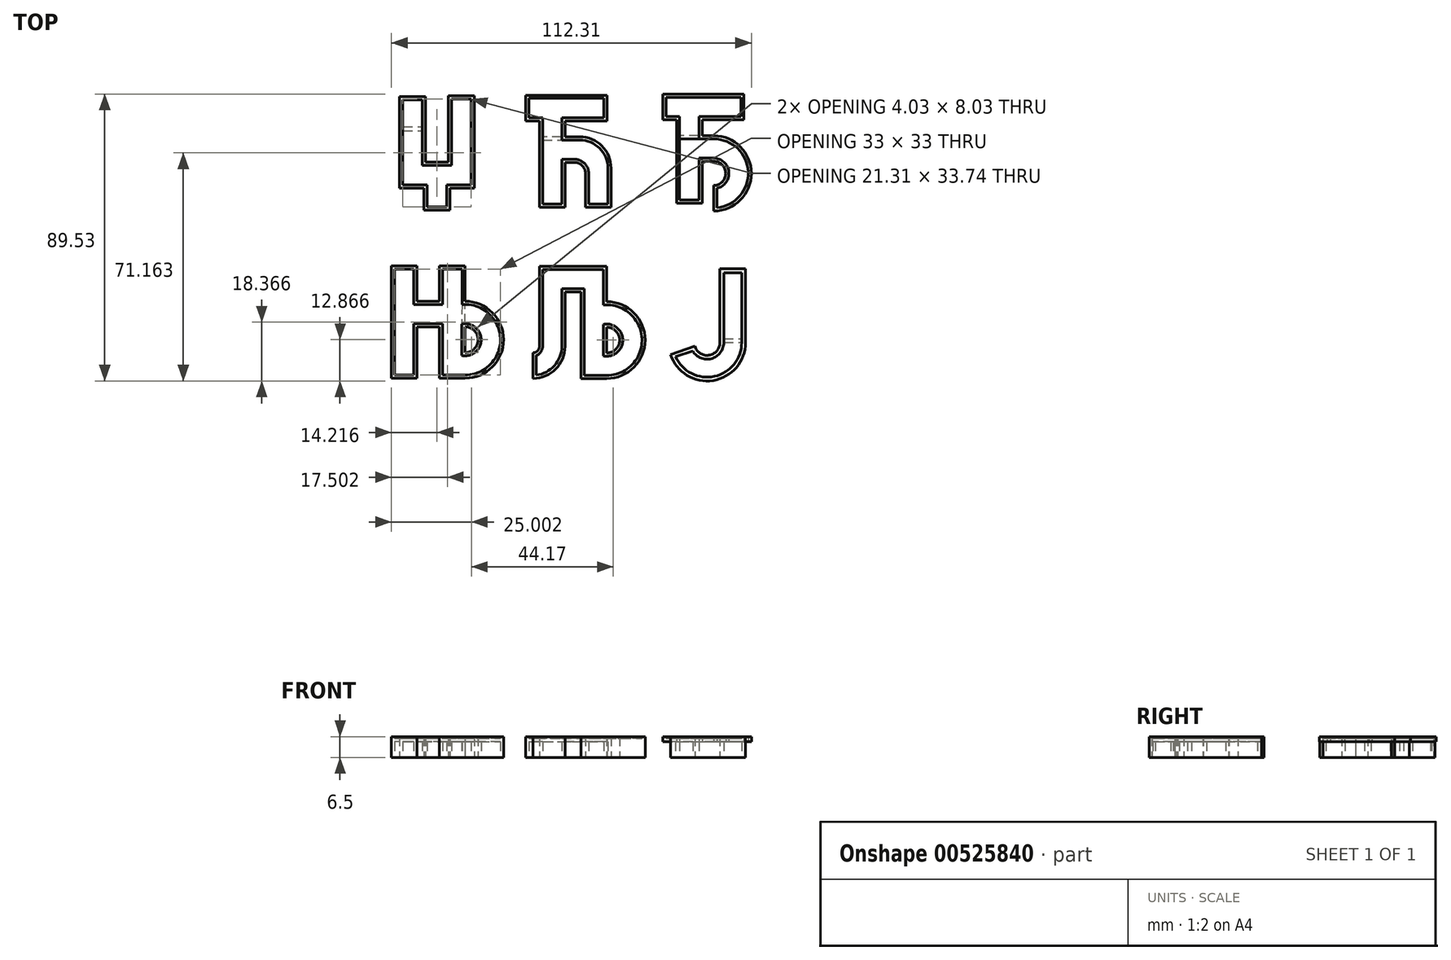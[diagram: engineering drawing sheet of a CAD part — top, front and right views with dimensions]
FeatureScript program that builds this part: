
annotation { "Feature Type Name" : "Feature", "Feature Type Description" : "" }
export const myFeature = defineFeature(function(context is Context, id is Id, definition is map)
    precondition{}
    {
        {
            var Q0;
            Q0=qCreatedBy(makeId("Top.planeOp"),FACE);
            var sketch = newSketch(context, id + "F0", { "sketchPlane" : qUnion([Q0])});
            skLineSegment(sketch, "E0", {"start": v(-54.27, 17.56) * mm, "end": v(-54.27, 46.23) * mm});
            skLineSegment(sketch, "E1", {"start": v(-54.27, 46.23) * mm, "end": v(-46.16, 46.23) * mm});
            skLineSegment(sketch, "E2", {"start": v(-46.16, 46.23) * mm, "end": v(-46.16, 25.68) * mm});
            skLineSegment(sketch, "E3", {"start": v(-46.16, 25.68) * mm, "end": v(-39.05, 25.68) * mm});
            skLineSegment(sketch, "E4", {"start": v(-39.05, 25.68) * mm, "end": v(-39.05, 46.48) * mm});
            skLineSegment(sketch, "E5", {"start": v(-39.05, 46.48) * mm, "end": v(-30.93, 46.48) * mm});
            skLineSegment(sketch, "E6", {"start": v(-30.93, 46.48) * mm, "end": v(-30.93, 17.56) * mm});
            skLineSegment(sketch, "E7", {"start": v(-30.93, 17.56) * mm, "end": v(-38.55, 17.56) * mm});
            skLineSegment(sketch, "E8", {"start": v(-38.55, 17.56) * mm, "end": v(-38.55, 10.7) * mm});
            skLineSegment(sketch, "E9", {"start": v(-38.55, 10.7) * mm, "end": v(-46.66, 10.7) * mm});
            skLineSegment(sketch, "E10", {"start": v(-46.66, 10.7) * mm, "end": v(-46.66, 17.56) * mm});
            skLineSegment(sketch, "E11", {"start": v(-46.66, 17.56) * mm, "end": v(-54.27, 17.56) * mm});
            skLineSegment(sketch, "E12.0", {"start": v(-31.95, 18.57) * mm, "end": v(-39.56, 18.57) * mm});
            skLineSegment(sketch, "E12.1", {"start": v(-53.26, 18.57) * mm, "end": v(-53.26, 45.21) * mm});
            skLineSegment(sketch, "E12.2", {"start": v(-45.65, 18.57) * mm, "end": v(-53.26, 18.57) * mm});
            skLineSegment(sketch, "E12.3", {"start": v(-45.65, 11.72) * mm, "end": v(-45.65, 18.57) * mm});
            skLineSegment(sketch, "E12.4", {"start": v(-39.56, 11.72) * mm, "end": v(-45.65, 11.72) * mm});
            skLineSegment(sketch, "E12.5", {"start": v(-53.26, 45.21) * mm, "end": v(-47.17, 45.21) * mm});
            skLineSegment(sketch, "E12.6", {"start": v(-39.56, 18.57) * mm, "end": v(-39.56, 11.72) * mm});
            skLineSegment(sketch, "E12.7", {"start": v(-47.17, 45.21) * mm, "end": v(-47.17, 24.66) * mm});
            skLineSegment(sketch, "E12.8", {"start": v(-47.17, 24.66) * mm, "end": v(-38.04, 24.66) * mm});
            skLineSegment(sketch, "E12.9", {"start": v(-38.04, 24.66) * mm, "end": v(-38.04, 45.46) * mm});
            skLineSegment(sketch, "E12.10", {"start": v(-38.04, 45.46) * mm, "end": v(-31.95, 45.46) * mm});
            skLineSegment(sketch, "E12.11", {"start": v(-31.95, 45.46) * mm, "end": v(-31.95, 18.57) * mm});
            skLineSegment(sketch, "E13", {"start": v(-53.26, 36.84) * mm, "end": v(-47.17, 36.84) * mm});
            skLineSegment(sketch, "E14", {"start": v(-53.26, 35.56) * mm, "end": v(-47.17, 35.56) * mm});
            skLineSegment(sketch, "E15", {"start": v(-45.65, 24.66) * mm, "end": v(-47.17, 24.66) * mm});
            skSolve(sketch);
        }
        {
            var Q0;
            Q0 = qSketchRegion(id + "F0", true);
            var Q1;
            Q1=makeQuery(id+"F0.imprint","IMPRINT",FACE,{"disambiguationData":[TD([[makeQuery(id+"F0.imprint","IMPRINT",EDGE,{"derivedFrom":sQuery(id+"F0.wireOp",EDGE,"E12.0")}),-1.0]])]});
            var Q2;
            {var subQ0=sQuery(id+"F0.wireOp",EDGE,"E13");Q2=makeQuery(id+"F0.imprint","IMPRINT",FACE,{"disambiguationData":[TD([[makeQuery(id+"F0.imprint","IMPRINT",EDGE,{"derivedFrom":subQ0}),-1.0]])]});}
            var Q3;
            {var subQ0=sQuery(id+"F0.wireOp",EDGE,"E12.5");Q3=makeQuery(id+"F0.imprint","IMPRINT",FACE,{"disambiguationData":[TD([[makeQuery(id+"F0.imprint","IMPRINT",EDGE,{"derivedFrom":subQ0}),-1.0]])]});}
            extrude(context, id + "F1", {"entities" : qUnion([Q0, Q1, Q2, Q3]), "depth" : 6 * mm, "offsetDistance" : 25 * mm});
        }
        {
            var Q0;
            Q0=makeQuery(id+"F0.imprint","IMPRINT",FACE,{"disambiguationData":[TD([[makeQuery(id+"F0.imprint","IMPRINT",EDGE,{"derivedFrom":sQuery(id+"F0.wireOp",EDGE,"E0")}),-1.0]])]});
            extrude(context, id + "F2", {"entities" : qUnion([Q0]), "operationType" : NewBodyOperationType.ADD, "depth" : 6.5 * mm, "offsetDistance" : 25 * mm});
        }
        {
            var Q0;
            Q0=makeQuery(id+"F0.imprint","IMPRINT",FACE,{"disambiguationData":[TD([[makeQuery(id+"F0.imprint","IMPRINT",EDGE,{"derivedFrom":sQuery(id+"F0.wireOp",EDGE,"E12.0")}),-1.0]])]});
            var Q1;
            {var subQ0=sQuery(id+"F0.wireOp",EDGE,"E12.5");Q1=makeQuery(id+"F0.imprint","IMPRINT",FACE,{"disambiguationData":[TD([[makeQuery(id+"F0.imprint","IMPRINT",EDGE,{"derivedFrom":subQ0}),-1.0]])]});}
            extrude(context, id + "F3", {"entities" : qUnion([Q0, Q1]), "operationType" : NewBodyOperationType.REMOVE, "depth" : 5 * mm, "offsetDistance" : 25 * mm});
        }
        {
            var Q0;
            Q0=qCreatedBy(makeId("Top.planeOp"),FACE);
            var sketch = newSketch(context, id + "F4", { "sketchPlane" : qUnion([Q0])});
            skLineSegment(sketch, "E16", {"start": v(-10.68, 38.61) * mm, "end": v(-10.68, 11.61) * mm});
            skLineSegment(sketch, "E17", {"start": v(-10.68, 11.61) * mm, "end": v(-2.68, 11.61) * mm});
            skLineSegment(sketch, "E18", {"start": v(-2.68, 11.61) * mm, "end": v(-2.68, 25.61) * mm});
            skLineSegment(sketch, "E19", {"start": v(-2.68, 25.61) * mm, "end": v(0.33, 25.61) * mm});
            skLineSegment(sketch, "E20", {"start": v(-10.68, 38.61) * mm, "end": v(-14.93, 38.61) * mm});
            skLineSegment(sketch, "E21", {"start": v(-14.93, 38.61) * mm, "end": v(-14.93, 46.61) * mm});
            skLineSegment(sketch, "E22", {"start": v(-14.93, 46.61) * mm, "end": v(10.4, 46.61) * mm});
            skLineSegment(sketch, "E23", {"start": v(10.4, 46.61) * mm, "end": v(10.4, 38.61) * mm});
            skLineSegment(sketch, "E24", {"start": v(10.4, 38.61) * mm, "end": v(-2.68, 38.61) * mm});
            skLineSegment(sketch, "E25", {"start": v(-2.68, 38.61) * mm, "end": v(-2.68, 33.61) * mm});
            skLineSegment(sketch, "E26", {"start": v(-2.68, 33.61) * mm, "end": v(1.92, 33.61) * mm});
            skArc(sketch, "E27", {"start": v(0.33, 25.61) * mm, "mid": v(2.86, 24.48) * mm, "end": v(3.7, 21.84) * mm});
            skArc(sketch, "E28", {"start": v(1.92, 33.61) * mm, "mid": v(8.84, 30.75) * mm, "end": v(11.7, 23.83) * mm});
            skLineSegment(sketch, "E29", {"start": v(3.7, 21.84) * mm, "end": v(3.7, 11.61) * mm});
            skLineSegment(sketch, "E30", {"start": v(11.7, 11.61) * mm, "end": v(11.7, 23.83) * mm});
            skLineSegment(sketch, "E31", {"start": v(11.7, 11.61) * mm, "end": v(3.7, 11.61) * mm});
            skLineSegment(sketch, "E32.0", {"start": v(9.4, 39.61) * mm, "end": v(-3.68, 39.61) * mm});
            skLineSegment(sketch, "E32.1", {"start": v(9.4, 45.61) * mm, "end": v(9.4, 39.61) * mm});
            skLineSegment(sketch, "E32.2", {"start": v(-13.93, 45.61) * mm, "end": v(9.4, 45.61) * mm});
            skLineSegment(sketch, "E32.3", {"start": v(-13.93, 39.61) * mm, "end": v(-13.93, 45.61) * mm});
            skLineSegment(sketch, "E32.4", {"start": v(-9.68, 39.61) * mm, "end": v(-13.93, 39.61) * mm});
            skLineSegment(sketch, "E32.5", {"start": v(10.7, 12.61) * mm, "end": v(4.7, 12.61) * mm});
            skLineSegment(sketch, "E32.6", {"start": v(10.7, 12.61) * mm, "end": v(10.7, 23.83) * mm});
            skArc(sketch, "E32.7", {"start": v(1.92, 32.61) * mm, "mid": v(8.13, 30.04) * mm, "end": v(10.7, 23.83) * mm});
            skLineSegment(sketch, "E32.8", {"start": v(-3.68, 32.61) * mm, "end": v(1.92, 32.61) * mm});
            skLineSegment(sketch, "E32.9", {"start": v(4.7, 21.8) * mm, "end": v(4.7, 12.61) * mm});
            skArc(sketch, "E32.10", {"start": v(0.33, 26.61) * mm, "mid": v(3.58, 25.17) * mm, "end": v(4.7, 21.8) * mm});
            skLineSegment(sketch, "E32.11", {"start": v(-3.68, 26.61) * mm, "end": v(0.33, 26.61) * mm});
            skLineSegment(sketch, "E32.12", {"start": v(-3.68, 12.61) * mm, "end": v(-3.68, 26.61) * mm});
            skLineSegment(sketch, "E32.13", {"start": v(-9.68, 12.61) * mm, "end": v(-3.68, 12.61) * mm});
            skLineSegment(sketch, "E32.14", {"start": v(-3.68, 39.61) * mm, "end": v(-3.68, 32.61) * mm});
            skLineSegment(sketch, "E32.15", {"start": v(-9.68, 39.61) * mm, "end": v(-9.68, 12.61) * mm});
            skLineSegment(sketch, "E33", {"start": v(-3.68, 32.61) * mm, "end": v(-9.68, 32.61) * mm});
            skLineSegment(sketch, "E34", {"start": v(-2.68, 33.61) * mm, "end": v(-9.68, 33.61) * mm});
            skSolve(sketch);
        }
        {
            var Q0;
            Q0 = qSketchRegion(id + "F4", true);
            var Q1;
            {var subQ1=sQuery(id+"F4.wireOp",EDGE,"E32.0");Q1=makeQuery(id+"F4.imprint","IMPRINT",FACE,{"disambiguationData":[TD([[makeQuery(id+"F4.imprint","IMPRINT",EDGE,{"derivedFrom":subQ1}),-1.0]])]});}
            var Q2;
            {var subQ0=sQuery(id+"F4.wireOp",EDGE,"E33");Q2=makeQuery(id+"F4.imprint","IMPRINT",FACE,{"disambiguationData":[TD([[makeQuery(id+"F4.imprint","IMPRINT",EDGE,{"derivedFrom":subQ0}),-1.0]])]});}
            var Q3;
            Q3=makeQuery(id+"F4.imprint","IMPRINT",FACE,{"disambiguationData":[TD([[makeQuery(id+"F4.imprint","IMPRINT",EDGE,{"derivedFrom":sQuery(id+"F4.wireOp",EDGE,"E32.5")}),-1.0]])]});
            extrude(context, id + "F5", {"entities" : qUnion([Q0, Q1, Q2, Q3]), "depth" : 6 * mm, "offsetDistance" : 25 * mm});
        }
        {
            var Q0;
            Q0=makeQuery(id+"F4.imprint","IMPRINT",FACE,{"disambiguationData":[TD([[makeQuery(id+"F4.imprint","IMPRINT",EDGE,{"derivedFrom":sQuery(id+"F4.wireOp",EDGE,"E16")}),1.0]])]});
            extrude(context, id + "F6", {"entities" : qUnion([Q0]), "operationType" : NewBodyOperationType.ADD, "depth" : 6.5 * mm, "offsetDistance" : 25 * mm});
        }
        {
            var Q0;
            {var subQ1=sQuery(id+"F4.wireOp",EDGE,"E32.0");Q0=makeQuery(id+"F4.imprint","IMPRINT",FACE,{"disambiguationData":[TD([[makeQuery(id+"F4.imprint","IMPRINT",EDGE,{"derivedFrom":subQ1}),-1.0]])]});}
            var Q1;
            Q1=makeQuery(id+"F4.imprint","IMPRINT",FACE,{"disambiguationData":[TD([[makeQuery(id+"F4.imprint","IMPRINT",EDGE,{"derivedFrom":sQuery(id+"F4.wireOp",EDGE,"E32.5")}),-1.0]])]});
            extrude(context, id + "F7", {"entities" : qUnion([Q0, Q1]), "operationType" : NewBodyOperationType.REMOVE, "depth" : 5 * mm, "offsetDistance" : 25 * mm});
        }
        {
            var Q0;
            Q0=qCreatedBy(makeId("Top.planeOp"),FACE);
            var sketch = newSketch(context, id + "F8", { "sketchPlane" : qUnion([Q0])});
            skLineSegment(sketch, "E35", {"start": v(32.1, 38.96) * mm, "end": v(32.1, 12.96) * mm});
            skLineSegment(sketch, "E36", {"start": v(32.1, 12.96) * mm, "end": v(40.1, 12.96) * mm});
            skLineSegment(sketch, "E37", {"start": v(40.1, 12.96) * mm, "end": v(40.1, 25.96) * mm});
            skLineSegment(sketch, "E38", {"start": v(40.1, 25.96) * mm, "end": v(43.74, 25.96) * mm});
            skLineSegment(sketch, "E39", {"start": v(32.1, 38.96) * mm, "end": v(27.86, 38.96) * mm});
            skLineSegment(sketch, "E40", {"start": v(27.86, 38.96) * mm, "end": v(27.86, 46.96) * mm});
            skLineSegment(sketch, "E41", {"start": v(27.86, 46.96) * mm, "end": v(53.19, 46.96) * mm});
            skLineSegment(sketch, "E42", {"start": v(53.19, 46.96) * mm, "end": v(53.19, 38.96) * mm});
            skLineSegment(sketch, "E43", {"start": v(53.19, 38.96) * mm, "end": v(40.1, 38.96) * mm});
            skLineSegment(sketch, "E44", {"start": v(40.1, 38.96) * mm, "end": v(40.1, 33.96) * mm});
            skLineSegment(sketch, "E45", {"start": v(40.1, 33.96) * mm, "end": v(43.74, 33.96) * mm});
            skLineSegment(sketch, "E46", {"start": v(43.74, 10.46) * mm, "end": v(43.74, 18.46) * mm});
            skArc(sketch, "E47", {"start": v(43.74, 33.96) * mm, "mid": v(55.49, 22.21) * mm, "end": v(43.74, 10.46) * mm});
            skArc(sketch, "E48", {"start": v(43.74, 25.96) * mm, "mid": v(47.49, 22.21) * mm, "end": v(43.74, 18.46) * mm});
            skLineSegment(sketch, "E49.0", {"start": v(52.19, 39.96) * mm, "end": v(39.1, 39.96) * mm});
            skLineSegment(sketch, "E49.1", {"start": v(52.19, 45.96) * mm, "end": v(52.19, 39.96) * mm});
            skLineSegment(sketch, "E49.2", {"start": v(28.86, 45.96) * mm, "end": v(52.19, 45.96) * mm});
            skArc(sketch, "E49.3", {"start": v(43.74, 26.96) * mm, "mid": v(48.46, 22.71) * mm, "end": v(44.74, 17.57) * mm});
            skLineSegment(sketch, "E49.4", {"start": v(44.74, 11.5) * mm, "end": v(44.74, 17.57) * mm});
            skArc(sketch, "E49.5", {"start": v(43.74, 32.96) * mm, "mid": v(54.47, 22.71) * mm, "end": v(44.74, 11.5) * mm});
            skLineSegment(sketch, "E49.6", {"start": v(39.1, 32.96) * mm, "end": v(43.74, 32.96) * mm});
            skLineSegment(sketch, "E49.7", {"start": v(39.1, 26.96) * mm, "end": v(43.74, 26.96) * mm});
            skLineSegment(sketch, "E49.8", {"start": v(39.1, 13.96) * mm, "end": v(39.1, 26.96) * mm});
            skLineSegment(sketch, "E49.9", {"start": v(33.1, 13.96) * mm, "end": v(39.1, 13.96) * mm});
            skLineSegment(sketch, "E49.10", {"start": v(39.1, 39.96) * mm, "end": v(39.1, 32.96) * mm});
            skLineSegment(sketch, "E49.11", {"start": v(33.1, 39.96) * mm, "end": v(33.1, 13.96) * mm});
            skLineSegment(sketch, "E49.12", {"start": v(33.1, 39.96) * mm, "end": v(28.86, 39.96) * mm});
            skLineSegment(sketch, "E49.13", {"start": v(28.86, 39.96) * mm, "end": v(28.86, 45.96) * mm});
            skLineSegment(sketch, "E50", {"start": v(39.1, 32.96) * mm, "end": v(33.1, 32.96) * mm});
            skLineSegment(sketch, "E51", {"start": v(40.1, 33.96) * mm, "end": v(33.1, 33.96) * mm});
            skSolve(sketch);
        }
        {
            var Q0;
            Q0 = qSketchRegion(id + "F8", true);
            var Q1;
            {var subQ5=sQuery(id+"F8.wireOp",EDGE,"E49.0");Q1=makeQuery(id+"F8.imprint","IMPRINT",FACE,{"disambiguationData":[TD([[makeQuery(id+"F8.imprint","IMPRINT",EDGE,{"derivedFrom":subQ5}),-1.0]])]});}
            var Q2;
            Q2=makeQuery(id+"F8.imprint","IMPRINT",FACE,{"disambiguationData":[TD([[makeQuery(id+"F8.imprint","IMPRINT",EDGE,{"derivedFrom":sQuery(id+"F8.wireOp",EDGE,"E35")}),1.0]])]});
            var Q3;
            {var subQ0=sQuery(id+"F8.wireOp",EDGE,"E50");Q3=makeQuery(id+"F8.imprint","IMPRINT",FACE,{"disambiguationData":[TD([[makeQuery(id+"F8.imprint","IMPRINT",EDGE,{"derivedFrom":subQ0}),-1.0]])]});}
            var Q4;
            Q4=makeQuery(id+"F8.imprint","IMPRINT",FACE,{"disambiguationData":[TD([[makeQuery(id+"F8.imprint","IMPRINT",EDGE,{"derivedFrom":sQuery(id+"F8.wireOp",EDGE,"E49.3")}),1.0]])]});
            extrude(context, id + "F9", {"entities" : qUnion([Q0, Q1, Q2, Q3, Q4]), "depth" : 6 * mm, "offsetDistance" : 25 * mm});
        }
        {
            var Q0;
            Q0=makeQuery(id+"F8.imprint","IMPRINT",FACE,{"disambiguationData":[TD([[makeQuery(id+"F8.imprint","IMPRINT",EDGE,{"derivedFrom":sQuery(id+"F8.wireOp",EDGE,"E35")}),1.0]])]});
            extrude(context, id + "F10", {"entities" : qUnion([Q0]), "operationType" : NewBodyOperationType.ADD, "depth" : 6.5 * mm, "offsetDistance" : 25 * mm});
        }
        {
            var Q0;
            {var subQ5=sQuery(id+"F8.wireOp",EDGE,"E49.0");Q0=makeQuery(id+"F8.imprint","IMPRINT",FACE,{"disambiguationData":[TD([[makeQuery(id+"F8.imprint","IMPRINT",EDGE,{"derivedFrom":subQ5}),-1.0]])]});}
            var Q1;
            Q1=makeQuery(id+"F8.imprint","IMPRINT",FACE,{"disambiguationData":[TD([[makeQuery(id+"F8.imprint","IMPRINT",EDGE,{"derivedFrom":sQuery(id+"F8.wireOp",EDGE,"E49.3")}),1.0]])]});
            extrude(context, id + "F11", {"entities" : qUnion([Q0, Q1]), "operationType" : NewBodyOperationType.REMOVE, "depth" : 5 * mm, "offsetDistance" : 25 * mm});
        }
        {
            var Q0;
            Q0=qCreatedBy(makeId("Top.planeOp"),FACE);
            var sketch = newSketch(context, id + "F12", { "sketchPlane" : qUnion([Q0])});
            skLineSegment(sketch, "E52", {"start": v(-56.82, -6.7) * mm, "end": v(-56.82, -41.7) * mm});
            skLineSegment(sketch, "E53", {"start": v(-56.82, -41.7) * mm, "end": v(-48.82, -41.7) * mm});
            skLineSegment(sketch, "E54", {"start": v(-48.82, -41.7) * mm, "end": v(-48.82, -25.7) * mm});
            skLineSegment(sketch, "E55", {"start": v(-48.82, -25.7) * mm, "end": v(-41.82, -25.7) * mm});
            skLineSegment(sketch, "E56", {"start": v(-41.82, -25.7) * mm, "end": v(-41.82, -41.7) * mm});
            skLineSegment(sketch, "E57", {"start": v(-41.82, -41.7) * mm, "end": v(-33.82, -41.7) * mm});
            skArc(sketch, "E58", {"start": v(-33.82, -41.7) * mm, "mid": v(-21.82, -29.7) * mm, "end": v(-33.82, -17.7) * mm});
            skLineSegment(sketch, "E59", {"start": v(-33.82, -17.7) * mm, "end": v(-33.82, -6.7) * mm});
            skLineSegment(sketch, "E60", {"start": v(-33.82, -6.7) * mm, "end": v(-41.82, -6.7) * mm});
            skLineSegment(sketch, "E61", {"start": v(-41.82, -6.7) * mm, "end": v(-41.82, -17.7) * mm});
            skLineSegment(sketch, "E62", {"start": v(-41.82, -17.7) * mm, "end": v(-48.82, -17.7) * mm});
            skLineSegment(sketch, "E63", {"start": v(-48.82, -17.7) * mm, "end": v(-48.82, -6.7) * mm});
            skLineSegment(sketch, "E64", {"start": v(-48.82, -6.7) * mm, "end": v(-56.82, -6.7) * mm});
            skArc(sketch, "E65.0", {"start": v(-33.83, -33.72) * mm, "mid": v(-29.8, -29.7) * mm, "end": v(-33.83, -25.69) * mm});
            skLineSegment(sketch, "E66", {"start": v(-33.83, -25.69) * mm, "end": v(-33.83, -33.72) * mm});
            skLineSegment(sketch, "E67.0", {"start": v(-49.82, -24.7) * mm, "end": v(-40.82, -24.7) * mm});
            skLineSegment(sketch, "E67.1", {"start": v(-49.82, -40.7) * mm, "end": v(-49.82, -24.7) * mm});
            skLineSegment(sketch, "E67.2", {"start": v(-34.82, -7.7) * mm, "end": v(-40.82, -7.7) * mm});
            skLineSegment(sketch, "E67.3", {"start": v(-34.82, -18.75) * mm, "end": v(-34.82, -7.7) * mm});
            skArc(sketch, "E67.4", {"start": v(-33.82, -40.7) * mm, "mid": v(-22.83, -29.2) * mm, "end": v(-34.82, -18.75) * mm});
            skLineSegment(sketch, "E67.5", {"start": v(-40.82, -40.7) * mm, "end": v(-33.82, -40.7) * mm});
            skLineSegment(sketch, "E67.6", {"start": v(-40.82, -7.7) * mm, "end": v(-40.82, -18.7) * mm});
            skLineSegment(sketch, "E67.7", {"start": v(-40.82, -18.7) * mm, "end": v(-49.82, -18.7) * mm});
            skLineSegment(sketch, "E67.8", {"start": v(-40.82, -24.7) * mm, "end": v(-40.82, -40.7) * mm});
            skLineSegment(sketch, "E67.9", {"start": v(-49.82, -18.7) * mm, "end": v(-49.82, -7.7) * mm});
            skLineSegment(sketch, "E67.10", {"start": v(-49.82, -7.7) * mm, "end": v(-55.82, -7.7) * mm});
            skLineSegment(sketch, "E67.11", {"start": v(-55.82, -7.7) * mm, "end": v(-55.82, -40.7) * mm});
            skLineSegment(sketch, "E67.12", {"start": v(-55.82, -40.7) * mm, "end": v(-49.82, -40.7) * mm});
            skArc(sketch, "E68.0", {"start": v(-34.83, -34.62) * mm, "mid": v(-28.8, -29.7) * mm, "end": v(-34.83, -24.8) * mm});
            skLineSegment(sketch, "E68.1", {"start": v(-34.83, -24.8) * mm, "end": v(-34.83, -34.62) * mm});
            skLineSegment(sketch, "E69", {"start": v(-34.82, -18.75) * mm, "end": v(-34.83, -24.8) * mm});
            skLineSegment(sketch, "E70", {"start": v(-33.83, -25.69) * mm, "end": v(-33.82, -17.7) * mm});
            skSolve(sketch);
        }
        {
            var Q0;
            Q0=makeQuery(id+"F12.imprint","IMPRINT",FACE,{"disambiguationData":[TD([[makeQuery(id+"F12.imprint","IMPRINT",EDGE,{"derivedFrom":sQuery(id+"F12.wireOp",EDGE,"E67.0")}),1.0]])]});
            var Q1;
            Q1=makeQuery(id+"F12.imprint","IMPRINT",FACE,{"disambiguationData":[TD([[makeQuery(id+"F12.imprint","IMPRINT",EDGE,{"derivedFrom":sQuery(id+"F12.wireOp",EDGE,"E65.0")}),-1.0]])]});
            var Q2;
            Q2=makeQuery(id+"F12.imprint","IMPRINT",FACE,{"disambiguationData":[TD([[makeQuery(id+"F12.imprint","IMPRINT",EDGE,{"derivedFrom":sQuery(id+"F12.wireOp",EDGE,"E52")}),1.0]])]});
            var Q3;
            {var subQ0=sQuery(id+"F12.wireOp",EDGE,"E69");Q3=makeQuery(id+"F12.imprint","IMPRINT",FACE,{"disambiguationData":[TD([[makeQuery(id+"F12.imprint","IMPRINT",EDGE,{"derivedFrom":subQ0}),1.0]])]});}
            extrude(context, id + "F13", {"entities" : qUnion([Q0, Q1, Q2, Q3]), "depth" : 6 * mm, "offsetDistance" : 25 * mm});
        }
        {
            var Q0;
            Q0=makeQuery(id+"F12.imprint","IMPRINT",FACE,{"disambiguationData":[TD([[makeQuery(id+"F12.imprint","IMPRINT",EDGE,{"derivedFrom":sQuery(id+"F12.wireOp",EDGE,"E52")}),1.0]])]});
            var Q1;
            Q1=makeQuery(id+"F12.imprint","IMPRINT",FACE,{"disambiguationData":[TD([[makeQuery(id+"F12.imprint","IMPRINT",EDGE,{"derivedFrom":sQuery(id+"F12.wireOp",EDGE,"E65.0")}),-1.0]])]});
            extrude(context, id + "F14", {"entities" : qUnion([Q0, Q1]), "operationType" : NewBodyOperationType.ADD, "depth" : 6.5 * mm, "offsetDistance" : 25 * mm});
        }
        {
            var Q0;
            Q0=makeQuery(id+"F12.imprint","IMPRINT",FACE,{"disambiguationData":[TD([[makeQuery(id+"F12.imprint","IMPRINT",EDGE,{"derivedFrom":sQuery(id+"F12.wireOp",EDGE,"E67.0")}),1.0]])]});
            extrude(context, id + "F15", {"entities" : qUnion([Q0]), "operationType" : NewBodyOperationType.REMOVE, "depth" : 5 * mm, "offsetDistance" : 25 * mm});
        }
        {
            var Q0;
            Q0=qCreatedBy(makeId("Top.planeOp"),FACE);
            var sketch = newSketch(context, id + "F16", { "sketchPlane" : qUnion([Q0])});
            skLineSegment(sketch, "E71", {"start": v(-2.66, -14.82) * mm, "end": v(2.35, -14.82) * mm});
            skLineSegment(sketch, "E72", {"start": v(2.35, -14.82) * mm, "end": v(2.35, -41.82) * mm});
            skLineSegment(sketch, "E73", {"start": v(2.35, -41.82) * mm, "end": v(10.35, -41.82) * mm});
            skArc(sketch, "E74", {"start": v(10.35, -41.82) * mm, "mid": v(22.35, -29.82) * mm, "end": v(10.35, -17.82) * mm});
            skLineSegment(sketch, "E75", {"start": v(10.35, -17.82) * mm, "end": v(10.35, -6.82) * mm});
            skArc(sketch, "E76.0", {"start": v(10.34, -33.84) * mm, "mid": v(14.37, -29.82) * mm, "end": v(10.34, -25.8) * mm});
            skLineSegment(sketch, "E77", {"start": v(10.34, -25.8) * mm, "end": v(10.34, -33.84) * mm});
            skLineSegment(sketch, "E78.0", {"start": v(-3.65, -13.82) * mm, "end": v(3.35, -13.82) * mm});
            skLineSegment(sketch, "E78.3", {"start": v(9.35, -18.87) * mm, "end": v(9.35, -7.82) * mm});
            skArc(sketch, "E78.4", {"start": v(10.35, -40.82) * mm, "mid": v(21.34, -29.32) * mm, "end": v(9.35, -18.87) * mm});
            skLineSegment(sketch, "E78.5", {"start": v(3.35, -40.82) * mm, "end": v(10.35, -40.82) * mm});
            skLineSegment(sketch, "E78.8", {"start": v(3.35, -13.82) * mm, "end": v(3.35, -40.82) * mm});
            skArc(sketch, "E79.0", {"start": v(9.34, -34.73) * mm, "mid": v(15.37, -29.82) * mm, "end": v(9.34, -24.9) * mm});
            skLineSegment(sketch, "E79.1", {"start": v(9.34, -24.9) * mm, "end": v(9.34, -34.73) * mm});
            skLineSegment(sketch, "E80", {"start": v(-10.66, -6.82) * mm, "end": v(10.35, -6.82) * mm});
            skLineSegment(sketch, "E81", {"start": v(-9.65, -7.82) * mm, "end": v(9.35, -7.82) * mm});
            skLineSegment(sketch, "E82", {"start": v(3.5, -31.78) * mm, "end": v(3.5, -31.78) * mm});
            skArc(sketch, "E83", {"start": v(-10.66, -31.78) * mm, "mid": v(-11.26, -33.2) * mm, "end": v(-12.7, -33.78) * mm});
            skLineSegment(sketch, "E84", {"start": v(-2.66, -14.82) * mm, "end": v(-2.66, -31.78) * mm});
            skArc(sketch, "E85.0", {"start": v(-2.66, -31.78) * mm, "mid": v(-5.6, -38.85) * mm, "end": v(-12.66, -41.78) * mm});
            skArc(sketch, "E86.0", {"start": v(-9.66, -31.78) * mm, "mid": v(-10.22, -33.52) * mm, "end": v(-11.7, -34.62) * mm});
            skLineSegment(sketch, "E86.1", {"start": v(4.5, -32.62) * mm, "end": v(4.5, -32.62) * mm});
            skArc(sketch, "E86.2", {"start": v(-3.66, -31.78) * mm, "mid": v(-5.97, -37.79) * mm, "end": v(-11.7, -40.72) * mm});
            skLineSegment(sketch, "E87", {"start": v(-9.66, -31.78) * mm, "end": v(-9.65, -7.82) * mm});
            skLineSegment(sketch, "E88", {"start": v(-3.65, -13.82) * mm, "end": v(-3.66, -31.78) * mm});
            skLineSegment(sketch, "E89", {"start": v(5.54, -29.78) * mm, "end": v(5.54, -29.78) * mm});
            skLineSegment(sketch, "E90", {"start": v(-11.7, -34.62) * mm, "end": v(-11.7, -40.72) * mm});
            skLineSegment(sketch, "E91", {"start": v(-10.66, -6.82) * mm, "end": v(-10.66, -31.78) * mm});
            skLineSegment(sketch, "E92", {"start": v(-12.7, -33.78) * mm, "end": v(-12.66, -41.78) * mm});
            skLineSegment(sketch, "E93", {"start": v(10.35, -17.82) * mm, "end": v(3.35, -17.8) * mm});
            skLineSegment(sketch, "E94", {"start": v(9.35, -18.87) * mm, "end": v(3.35, -18.85) * mm});
            skSolve(sketch);
        }
        {
            var Q0;
            Q0 = qSketchRegion(id + "F16", true);
            var Q1;
            Q1=makeQuery(id+"F16.imprint","IMPRINT",FACE,{"disambiguationData":[TD([[makeQuery(id+"F16.imprint","IMPRINT",EDGE,{"derivedFrom":sQuery(id+"F16.wireOp",EDGE,"E78.4")}),1.0]])]});
            var Q2;
            Q2=makeQuery(id+"F16.imprint","IMPRINT",FACE,{"disambiguationData":[TD([[makeQuery(id+"F16.imprint","IMPRINT",EDGE,{"derivedFrom":sQuery(id+"F16.wireOp",EDGE,"E76.0")}),-1.0]])]});
            var Q3;
            {var subQ0=sQuery(id+"F16.wireOp",EDGE,"E94");Q3=makeQuery(id+"F16.imprint","IMPRINT",FACE,{"disambiguationData":[TD([[makeQuery(id+"F16.imprint","IMPRINT",EDGE,{"derivedFrom":subQ0}),-1.0]])]});}
            var Q4;
            {var subQ1=sQuery(id+"F16.wireOp",EDGE,"E78.0");Q4=makeQuery(id+"F16.imprint","IMPRINT",FACE,{"disambiguationData":[TD([[makeQuery(id+"F16.imprint","IMPRINT",EDGE,{"derivedFrom":subQ1}),1.0]])]});}
            extrude(context, id + "F17", {"entities" : qUnion([Q0, Q1, Q2, Q3, Q4]), "depth" : 6 * mm, "offsetDistance" : 25 * mm});
        }
        {
            var Q0;
            Q0=makeQuery(id+"F16.imprint","IMPRINT",FACE,{"disambiguationData":[TD([[makeQuery(id+"F16.imprint","IMPRINT",EDGE,{"derivedFrom":sQuery(id+"F16.wireOp",EDGE,"E71")}),1.0]])]});
            var Q1;
            Q1=makeQuery(id+"F16.imprint","IMPRINT",FACE,{"disambiguationData":[TD([[makeQuery(id+"F16.imprint","IMPRINT",EDGE,{"derivedFrom":sQuery(id+"F16.wireOp",EDGE,"E76.0")}),-1.0]])]});
            extrude(context, id + "F18", {"entities" : qUnion([Q0, Q1]), "operationType" : NewBodyOperationType.ADD, "depth" : 6.5 * mm, "offsetDistance" : 25 * mm});
        }
        {
            var Q0;
            {var subQ1=sQuery(id+"F16.wireOp",EDGE,"E78.0");Q0=makeQuery(id+"F16.imprint","IMPRINT",FACE,{"disambiguationData":[TD([[makeQuery(id+"F16.imprint","IMPRINT",EDGE,{"derivedFrom":subQ1}),1.0]])]});}
            var Q1;
            Q1=makeQuery(id+"F16.imprint","IMPRINT",FACE,{"disambiguationData":[TD([[makeQuery(id+"F16.imprint","IMPRINT",EDGE,{"derivedFrom":sQuery(id+"F16.wireOp",EDGE,"E78.4")}),1.0]])]});
            extrude(context, id + "F19", {"entities" : qUnion([Q0, Q1]), "operationType" : NewBodyOperationType.ADD, "depth" : 5 * mm, "offsetDistance" : 25 * mm});
        }
        {
            var Q0;
            Q0=qCreatedBy(makeId("Top.planeOp"),FACE);
            var sketch = newSketch(context, id + "F20", { "sketchPlane" : qUnion([Q0])});
            skLineSegment(sketch, "E95", {"start": v(45.66, -7.57) * mm, "end": v(45.66, -30.57) * mm});
            skLineSegment(sketch, "E96", {"start": v(45.66, -7.57) * mm, "end": v(53.66, -7.57) * mm});
            skLineSegment(sketch, "E97", {"start": v(53.66, -7.57) * mm, "end": v(53.66, -30.57) * mm});
            skArc(sketch, "E98", {"start": v(30.25, -34.3) * mm, "mid": v(43.55, -42.42) * mm, "end": v(53.66, -30.57) * mm});
            skArc(sketch, "E99", {"start": v(37.84, -31.74) * mm, "mid": v(42.25, -34.53) * mm, "end": v(45.66, -30.57) * mm});
            skLineSegment(sketch, "E100", {"start": v(37.84, -31.74) * mm, "end": v(30.25, -34.3) * mm});
            skLineSegment(sketch, "E101.0", {"start": v(37.19, -33.22) * mm, "end": v(31.83, -35.03) * mm});
            skLineSegment(sketch, "E101.1", {"start": v(46.86, -8.77) * mm, "end": v(46.86, -30.57) * mm});
            skLineSegment(sketch, "E101.2", {"start": v(46.86, -8.77) * mm, "end": v(52.46, -8.77) * mm});
            skArc(sketch, "E101.3", {"start": v(37.19, -33.22) * mm, "mid": v(43.04, -35.59) * mm, "end": v(46.86, -30.57) * mm});
            skLineSegment(sketch, "E101.4", {"start": v(52.46, -8.77) * mm, "end": v(52.46, -30.57) * mm});
            skArc(sketch, "E101.5", {"start": v(31.83, -35.03) * mm, "mid": v(43.94, -41.13) * mm, "end": v(52.46, -30.57) * mm});
            skLineSegment(sketch, "E102", {"start": v(46.86, -30.57) * mm, "end": v(52.46, -30.57) * mm});
            skLineSegment(sketch, "E103", {"start": v(46.86, -29.37) * mm, "end": v(52.46, -29.37) * mm});
            skSolve(sketch);
        }
        {
            var Q0;
            {var subQ0=sQuery(id+"F20.wireOp",EDGE,"E101.2");Q0=makeQuery(id+"F20.imprint","IMPRINT",FACE,{"disambiguationData":[TD([[makeQuery(id+"F20.imprint","IMPRINT",EDGE,{"derivedFrom":subQ0}),-1.0]])]});}
            var Q1;
            {var subQ0=sQuery(id+"F20.wireOp",EDGE,"E102");Q1=makeQuery(id+"F20.imprint","IMPRINT",FACE,{"disambiguationData":[TD([[makeQuery(id+"F20.imprint","IMPRINT",EDGE,{"derivedFrom":subQ0}),1.0]])]});}
            var Q2;
            Q2=makeQuery(id+"F20.imprint","IMPRINT",FACE,{"disambiguationData":[TD([[makeQuery(id+"F20.imprint","IMPRINT",EDGE,{"derivedFrom":sQuery(id+"F20.wireOp",EDGE,"E101.0")}),1.0]])]});
            var Q3;
            Q3=makeQuery(id+"F20.imprint","IMPRINT",FACE,{"disambiguationData":[TD([[makeQuery(id+"F20.imprint","IMPRINT",EDGE,{"derivedFrom":sQuery(id+"F20.wireOp",EDGE,"E95")}),1.0]])]});
            extrude(context, id + "F21", {"entities" : qUnion([Q0, Q1, Q2, Q3]), "depth" : 6 * mm, "offsetDistance" : 25 * mm});
        }
        {
            var Q0;
            Q0=makeQuery(id+"F20.imprint","IMPRINT",FACE,{"disambiguationData":[TD([[makeQuery(id+"F20.imprint","IMPRINT",EDGE,{"derivedFrom":sQuery(id+"F20.wireOp",EDGE,"E95")}),1.0]])]});
            extrude(context, id + "F22", {"entities" : qUnion([Q0]), "operationType" : NewBodyOperationType.ADD, "depth" : 6.5 * mm, "offsetDistance" : 25 * mm});
        }
        {
            var Q0;
            {var subQ0=sQuery(id+"F20.wireOp",EDGE,"E101.2");Q0=makeQuery(id+"F20.imprint","IMPRINT",FACE,{"disambiguationData":[TD([[makeQuery(id+"F20.imprint","IMPRINT",EDGE,{"derivedFrom":subQ0}),-1.0]])]});}
            var Q1;
            Q1=makeQuery(id+"F20.imprint","IMPRINT",FACE,{"disambiguationData":[TD([[makeQuery(id+"F20.imprint","IMPRINT",EDGE,{"derivedFrom":sQuery(id+"F20.wireOp",EDGE,"E101.0")}),1.0]])]});
            extrude(context, id + "F23", {"entities" : qUnion([Q0, Q1]), "operationType" : NewBodyOperationType.REMOVE, "depth" : 5 * mm, "offsetDistance" : 25 * mm});
        }
    });
